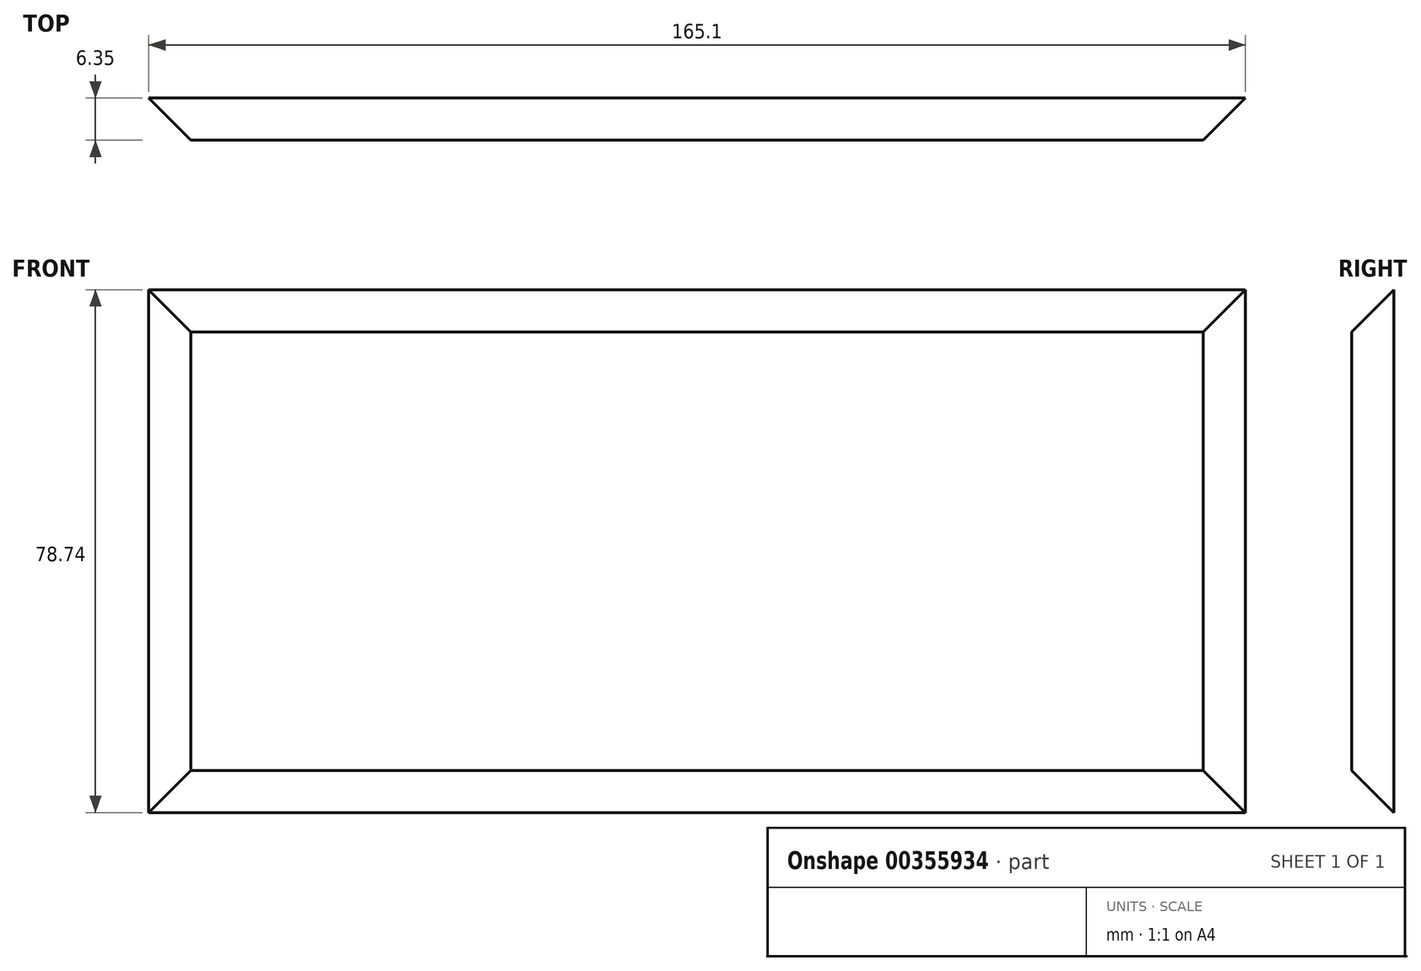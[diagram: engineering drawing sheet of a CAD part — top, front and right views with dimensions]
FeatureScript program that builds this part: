
annotation { "Feature Type Name" : "Feature", "Feature Type Description" : "" }
export const myFeature = defineFeature(function(context is Context, id is Id, definition is map)
    precondition{}
    {
        {
            var Q0;
            Q0=qCreatedBy(makeId("Front.planeOp"),FACE);
            var sketch = newSketch(context, id + "F0", { "sketchPlane" : qUnion([Q0])});
            skPoint(sketch, "E0.middle", {"position": v(0, 0) * mm});
            skLineSegment(sketch, "E1.0", {"start": v(82.55, 39.37) * mm, "end": v(-82.55, 39.37) * mm});
            skLineSegment(sketch, "E1.1", {"start": v(82.55, -39.37) * mm, "end": v(82.55, 39.37) * mm});
            skLineSegment(sketch, "E1.2", {"start": v(82.55, -39.37) * mm, "end": v(-82.55, -39.37) * mm});
            skLineSegment(sketch, "E1.3", {"start": v(-82.55, -39.37) * mm, "end": v(-82.55, 39.37) * mm});
            skPoint(sketch, "E0.left.end.orphan", {"position": v(88.9, 45.72) * mm});
            skPoint(sketch, "E0.bottom.start.orphan", {"position": v(88.9, -45.72) * mm});
            skPoint(sketch, "E0.right.end.orphan", {"position": v(-88.9, 45.72) * mm});
            skPoint(sketch, "E0.right.start.orphan", {"position": v(-88.9, -45.72) * mm});
            skSolve(sketch);
        }
        {
            var Q0;
            Q0=qSketchRegion(id+"F0",true);
            extrude(context, id + "F1", {"entities" : qUnion([Q0]), "depth" : 6.35 * mm});
        }
        {
            var Q0;
            Q0=makeQuery(id+"F1.opExtrude","CAP_FACE",FACE,{"disambiguationData":[OSD([sQuery(id+"F0.wireOp",EDGE,"E1.0"),sQuery(id+"F0.wireOp",EDGE,"E1.1"),sQuery(id+"F0.wireOp",EDGE,"E1.2"),sQuery(id+"F0.wireOp",EDGE,"E1.3")])],"isStart":false});
            chamfer(context, id + "F2", {"entities" : qUnion([Q0]), "width" : 6.35 * mm, "tangentPropagation" : true});
        }
    });
